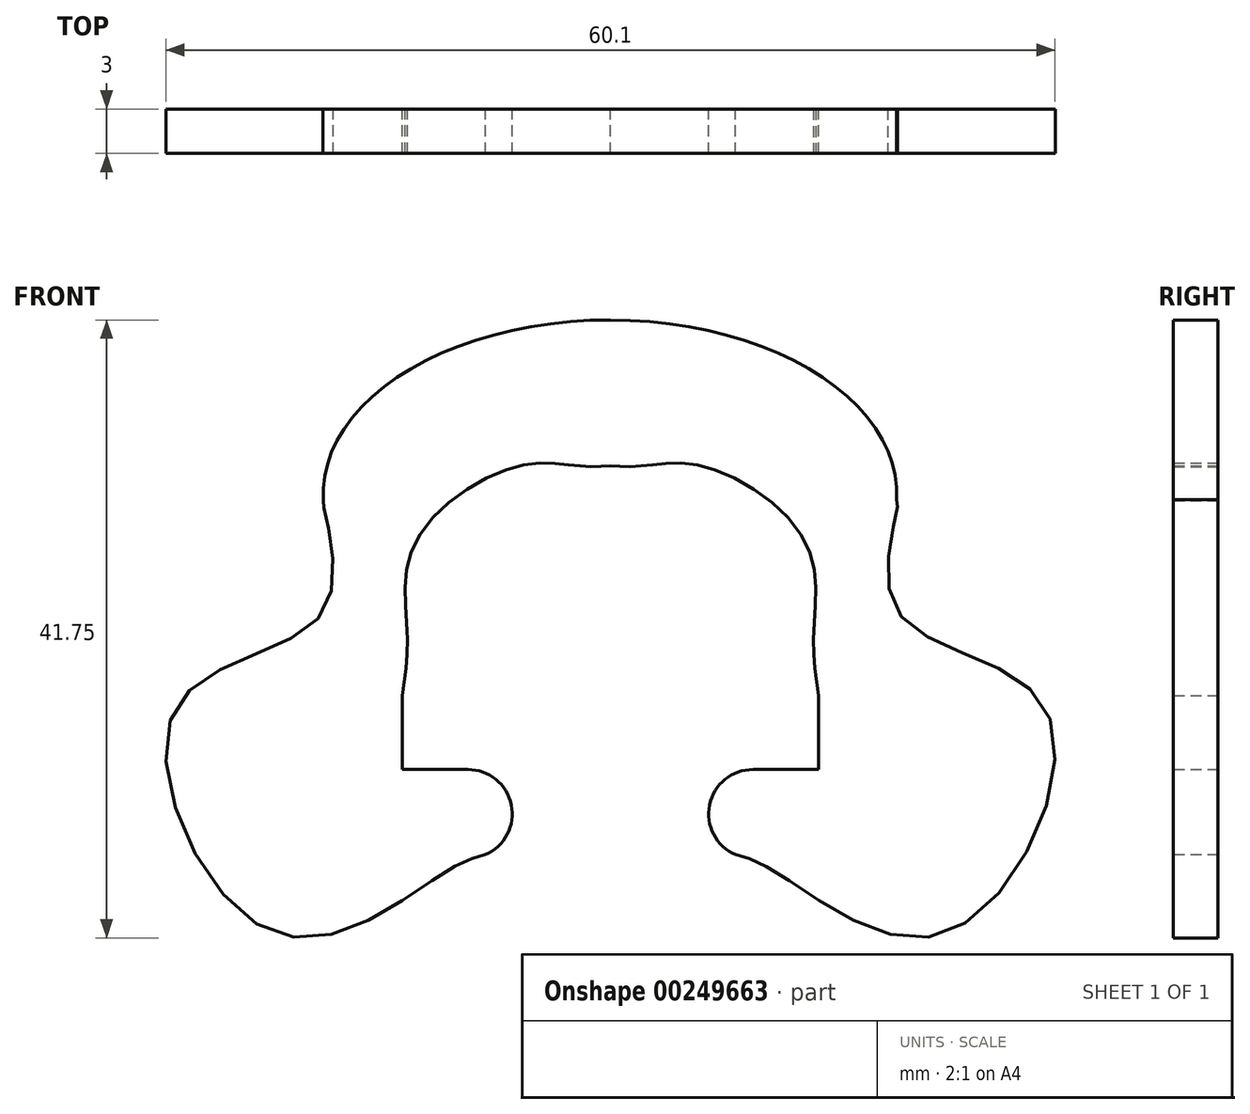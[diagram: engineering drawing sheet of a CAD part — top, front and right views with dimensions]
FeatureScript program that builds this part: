
annotation { "Feature Type Name" : "Feature", "Feature Type Description" : "" }
export const myFeature = defineFeature(function(context is Context, id is Id, definition is map)
    precondition{}
    {
        {
            var Q0;
            Q0=qCreatedBy(makeId("Front.planeOp"),FACE);
            var sketch = newSketch(context, id + "F0", { "sketchPlane" : qUnion([Q0])});
            skLineSegment(sketch, "E0", {"start": v(-14.07, -11.08) * mm, "end": v(-9.64, -11.08) * mm});
            skLineSegment(sketch, "E1", {"start": v(-14.07, -11.08) * mm, "end": v(-14.07, -6.08) * mm});
            skFitSpline(sketch, "E2", {"points": [v(-14.07, -6.08) * mm, v(-13.73, -2) * mm, v(-13.2, 4.24) * mm, v(-6.22, 9.41) * mm, v(-2.06, 9.42) * mm, v(0, 9.43) * mm]});
            skFitSpline(sketch, "E3", {"points": [v(14.07, -6.08) * mm, v(13.73, -2) * mm, v(13.2, 4.24) * mm, v(6.22, 9.41) * mm, v(2.06, 9.42) * mm, v(0, 9.43) * mm]});
            skLineSegment(sketch, "E4", {"start": v(14.07, -11.08) * mm, "end": v(14.07, -6.08) * mm});
            skFitSpline(sketch, "E5", {"points": [v(0, 19.3) * mm, v(0, 19.3) * mm, v(0, 19.3) * mm, v(0, 19.3) * mm]});
            skFitSpline(sketch, "E6", {"points": [v(0, 19.3) * mm, v(0, 19.3) * mm, v(0, 19.3) * mm, v(0, 19.3) * mm]});
            skFitSpline(sketch, "E7", {"points": [v(-19.4, 7.08) * mm, v(-19.39, 6.68) * mm, v(-19.41, -0.42) * mm, v(-29.48, -7.1) * mm, v(-22.59, -22.15) * mm, v(-11.2, -18.02) * mm, v(-8.45, -16.83) * mm]});
            skEllipticalArc(sketch, "E8", {});
            skArc(sketch, "E9", {"start": v(-8.45, -16.83) * mm, "mid": v(-6.7, -13.47) * mm, "end": v(-9.64, -11.08) * mm});
            skLineSegment(sketch, "E10", {"start": v(14.07, -11.08) * mm, "end": v(9.64, -11.08) * mm});
            skFitSpline(sketch, "E11", {"points": [v(19.34, 7.16) * mm, v(19.39, 6.68) * mm, v(19.41, -0.42) * mm, v(29.48, -7.1) * mm, v(22.59, -22.15) * mm, v(11.2, -18.02) * mm, v(8.45, -16.83) * mm]});
            skArc(sketch, "E12", {"start": v(9.64, -11.08) * mm, "mid": v(6.7, -13.47) * mm, "end": v(8.45, -16.83) * mm});
            const initialGuessF0  = {"E8": [-3.519899999999154e-05, 0.007508284000000003, 19.383563, 0, 0.019383563, 0.01178365, 6.253754, 9.461088]};
            skSetInitialGuess(sketch, initialGuessF0);
            skSolve(sketch);
        }
        {
            var Q0;
            Q0 = qSketchRegion(id + "F0", true);
            extrude(context, id + "F1", {"entities" : qUnion([Q0]), "depth" : 3 * mm});
        }
    });
